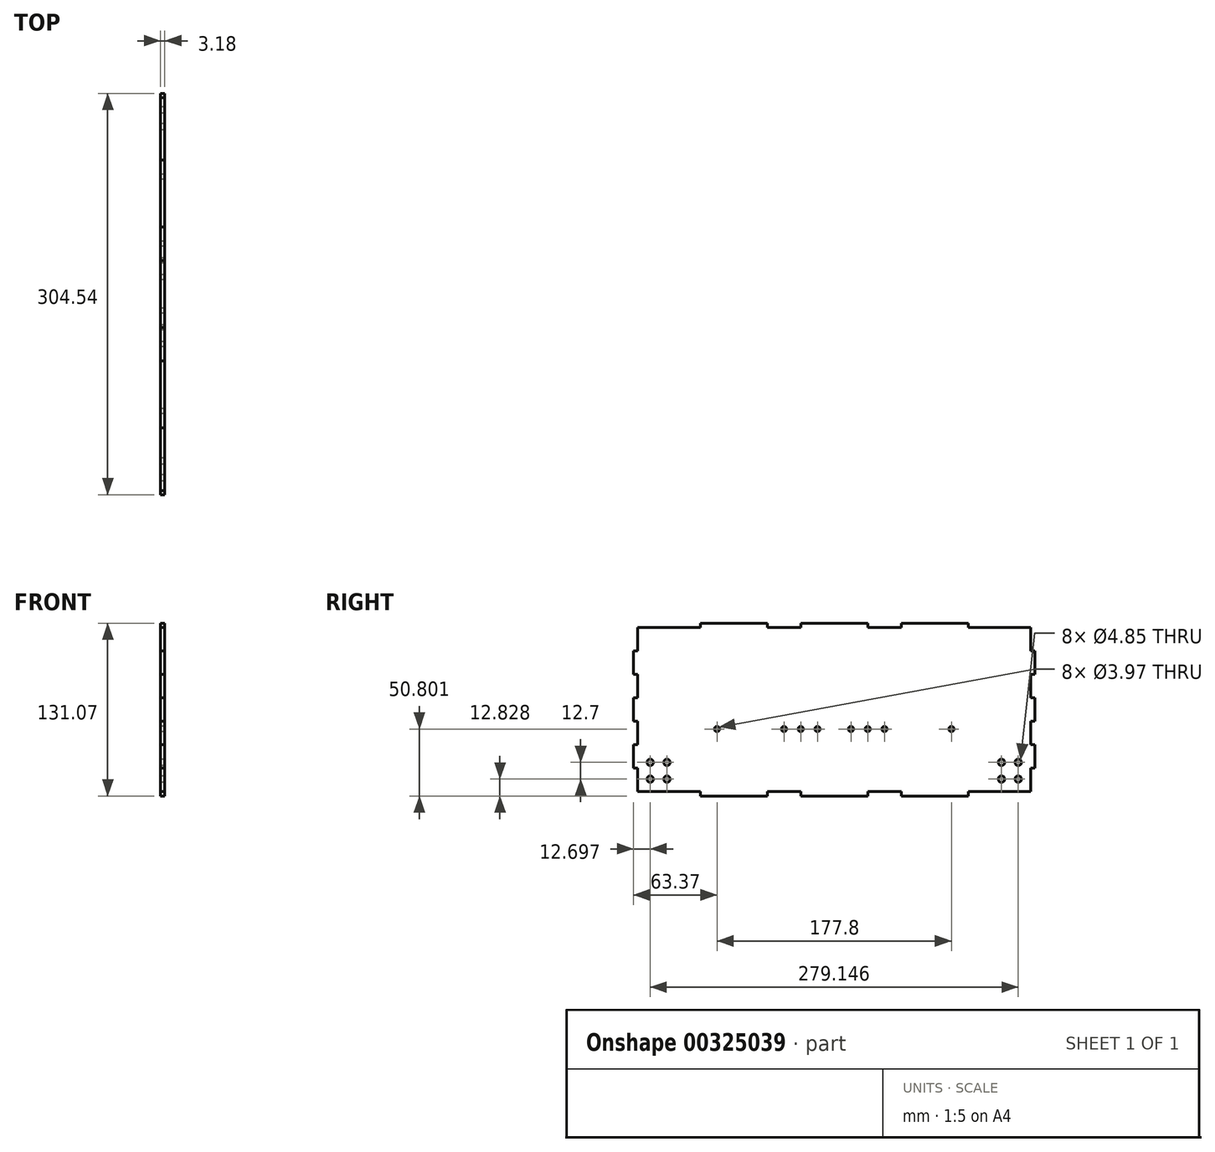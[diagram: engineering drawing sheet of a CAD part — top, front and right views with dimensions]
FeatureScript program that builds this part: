
annotation { "Feature Type Name" : "Feature", "Feature Type Description" : "" }
export const myFeature = defineFeature(function(context is Context, id is Id, definition is map)
    precondition{}
    {
        {
            var Q0;
            Q0=qCreatedBy(makeId("Right.planeOp"),FACE);
            var sketch = newSketch(context, id + "F0", { "sketchPlane" : qUnion([Q0])});
            skLineSegment(sketch, "E0.MirrorCS", {"start": v(-50.8, -81.48) * mm, "end": v(-50.8, -78.18) * mm});
            skLineSegment(sketch, "E1.MirrorCS", {"start": v(25.4, -81.48) * mm, "end": v(25.4, -78.18) * mm});
            skLineSegment(sketch, "E2.MirrorCS", {"start": v(50.8, -81.48) * mm, "end": v(50.8, -78.18) * mm});
            skLineSegment(sketch, "E3.MirrorCS", {"start": v(101.6, -81.48) * mm, "end": v(101.6, -78.18) * mm});
            skLineSegment(sketch, "E4.MirrorCS", {"start": v(-25.4, -81.48) * mm, "end": v(-25.4, -78.18) * mm});
            skLineSegment(sketch, "E5.MirrorCS", {"start": v(101.6, -81.48) * mm, "end": v(50.8, -81.48) * mm});
            skLineSegment(sketch, "E6.MirrorCS", {"start": v(-25.4, -81.48) * mm, "end": v(25.4, -81.48) * mm});
            skLineSegment(sketch, "E7.MirrorCS", {"start": v(-50.8, -81.48) * mm, "end": v(-25.4, -81.48) * mm, "construction": true});
            skLineSegment(sketch, "E8.MirrorCS", {"start": v(-101.6, -81.48) * mm, "end": v(-50.8, -81.48) * mm});
            skLineSegment(sketch, "E9.MirrorCS", {"start": v(-101.6, -81.48) * mm, "end": v(-101.6, -78.18) * mm});
            skLineSegment(sketch, "E10", {"start": v(101.6, -78.18) * mm, "end": v(149.1, -78.18) * mm});
            skLineSegment(sketch, "E11", {"start": v(50.8, -78.18) * mm, "end": v(25.4, -78.18) * mm});
            skLineSegment(sketch, "E12", {"start": v(-25.4, -78.18) * mm, "end": v(-50.8, -78.18) * mm});
            skLineSegment(sketch, "E13.MirrorCS", {"start": v(-101.6, -78.18) * mm, "end": v(-149.1, -78.18) * mm});
            skLineSegment(sketch, "E14", {"start": v(-149.1, -78.18) * mm, "end": v(-149.1, -60.4) * mm});
            skLineSegment(sketch, "E15", {"start": v(149.1, 46.28) * mm, "end": v(149.1, 28.5) * mm});
            skLineSegment(sketch, "E16", {"start": v(149.1, -15.95) * mm, "end": v(-149.1, -15.95) * mm, "construction": true});
            skLineSegment(sketch, "E17.MirrorCS", {"start": v(-50.8, 49.59) * mm, "end": v(-25.4, 49.59) * mm, "construction": true});
            skLineSegment(sketch, "E18.MirrorCS", {"start": v(-101.6, 49.59) * mm, "end": v(-101.6, 46.28) * mm});
            skLineSegment(sketch, "E19.MirrorCS", {"start": v(50.8, 46.28) * mm, "end": v(25.4, 46.28) * mm});
            skLineSegment(sketch, "E20.MirrorCS", {"start": v(25.4, 49.59) * mm, "end": v(25.4, 46.28) * mm});
            skLineSegment(sketch, "E21.MirrorCS", {"start": v(101.6, 49.59) * mm, "end": v(101.6, 46.28) * mm});
            skLineSegment(sketch, "E22.MirrorCS", {"start": v(101.6, 49.59) * mm, "end": v(50.8, 49.59) * mm});
            skLineSegment(sketch, "E23.MirrorCS", {"start": v(-101.6, 49.59) * mm, "end": v(-50.8, 49.59) * mm});
            skLineSegment(sketch, "E24.MirrorCS", {"start": v(-25.4, 46.28) * mm, "end": v(-50.8, 46.28) * mm});
            skLineSegment(sketch, "E25.MirrorCS", {"start": v(-101.6, 46.28) * mm, "end": v(-149.1, 46.28) * mm});
            skLineSegment(sketch, "E26.MirrorCS", {"start": v(101.6, 46.28) * mm, "end": v(149.1, 46.28) * mm});
            skLineSegment(sketch, "E27.MirrorCS", {"start": v(-50.8, 49.59) * mm, "end": v(-50.8, 46.28) * mm});
            skLineSegment(sketch, "E28.MirrorCS", {"start": v(50.8, 49.59) * mm, "end": v(50.8, 46.28) * mm});
            skLineSegment(sketch, "E29.MirrorCS", {"start": v(-25.4, 49.59) * mm, "end": v(-25.4, 46.28) * mm});
            skLineSegment(sketch, "E30.MirrorCS", {"start": v(-25.4, 49.59) * mm, "end": v(25.4, 49.59) * mm});
            skPoint(sketch, "E31", {"position": v(0, -30.68) * mm});
            skPoint(sketch, "E32", {"position": v(0, -15.95) * mm});
            skCircle(sketch, "E33", {"center": v(38.1, -30.68) * mm, "radius": 1.98 * mm});
            skCircle(sketch, "E34.MirrorC", {"center": v(-38.1, -30.68) * mm, "radius": 1.98 * mm});
            skCircle(sketch, "E35", {"center": v(88.9, -30.68) * mm, "radius": 1.98 * mm});
            skCircle(sketch, "E36.MirrorC", {"center": v(-88.9, -30.68) * mm, "radius": 1.98 * mm});
            skLineSegment(sketch, "E37", {"start": v(-149.1, 28.5) * mm, "end": v(-152.27, 28.5) * mm});
            skLineSegment(sketch, "E38", {"start": v(-152.27, 28.5) * mm, "end": v(-152.27, 10.72) * mm});
            skLineSegment(sketch, "E39", {"start": v(-152.27, 10.72) * mm, "end": v(-149.1, 10.72) * mm});
            skLineSegment(sketch, "E40", {"start": v(-149.1, -7.06) * mm, "end": v(-152.27, -7.06) * mm});
            skLineSegment(sketch, "E41", {"start": v(-152.27, -7.06) * mm, "end": v(-152.27, -24.84) * mm});
            skLineSegment(sketch, "E42", {"start": v(-152.27, -24.84) * mm, "end": v(-149.1, -24.84) * mm});
            skLineSegment(sketch, "E43", {"start": v(-149.1, -42.62) * mm, "end": v(-152.27, -42.62) * mm});
            skLineSegment(sketch, "E44", {"start": v(-152.27, -42.62) * mm, "end": v(-152.27, -60.4) * mm});
            skLineSegment(sketch, "E45", {"start": v(-152.27, -60.4) * mm, "end": v(-149.1, -60.4) * mm});
            skLineSegment(sketch, "E46", {"start": v(-152.27, 10.72) * mm, "end": v(-152.27, -7.06) * mm, "construction": true});
            skLineSegment(sketch, "E47", {"start": v(-152.27, -24.84) * mm, "end": v(-152.27, -42.62) * mm, "construction": true});
            skLineSegment(sketch, "E48", {"start": v(-152.27, 28.5) * mm, "end": v(-152.27, 46.28) * mm, "construction": true});
            skLineSegment(sketch, "E49", {"start": v(-152.27, -60.4) * mm, "end": v(-152.27, -78.18) * mm, "construction": true});
            skLineSegment(sketch, "E50.trimOffspring", {"start": v(-149.1, 28.5) * mm, "end": v(-149.1, 46.28) * mm});
            skLineSegment(sketch, "E51.trimOffspring", {"start": v(-149.1, -7.06) * mm, "end": v(-149.1, 10.72) * mm});
            skLineSegment(sketch, "E52.trimOffspring", {"start": v(-149.1, -42.62) * mm, "end": v(-149.1, -24.84) * mm});
            skLineSegment(sketch, "E53.MirrorCS", {"start": v(152.27, 10.72) * mm, "end": v(152.27, -7.06) * mm, "construction": true});
            skLineSegment(sketch, "E54.MirrorCS", {"start": v(149.1, -42.62) * mm, "end": v(149.1, -24.84) * mm});
            skLineSegment(sketch, "E55.MirrorCS", {"start": v(152.27, 28.5) * mm, "end": v(152.27, 10.72) * mm});
            skLineSegment(sketch, "E56.MirrorCS", {"start": v(152.27, -24.84) * mm, "end": v(152.27, -42.62) * mm, "construction": true});
            skLineSegment(sketch, "E57.MirrorCS", {"start": v(152.27, 10.72) * mm, "end": v(149.1, 10.72) * mm});
            skLineSegment(sketch, "E58.MirrorCS", {"start": v(149.1, -7.06) * mm, "end": v(152.27, -7.06) * mm});
            skLineSegment(sketch, "E59.MirrorCS", {"start": v(152.27, -7.06) * mm, "end": v(152.27, -24.84) * mm});
            skLineSegment(sketch, "E60.MirrorCS", {"start": v(152.27, -24.84) * mm, "end": v(149.1, -24.84) * mm});
            skLineSegment(sketch, "E61.MirrorCS", {"start": v(149.1, -42.62) * mm, "end": v(152.27, -42.62) * mm});
            skLineSegment(sketch, "E62.MirrorCS", {"start": v(149.1, -7.06) * mm, "end": v(149.1, 10.72) * mm});
            skLineSegment(sketch, "E63.MirrorCS", {"start": v(152.27, -42.62) * mm, "end": v(152.27, -60.4) * mm});
            skLineSegment(sketch, "E64.MirrorCS", {"start": v(152.27, -60.4) * mm, "end": v(149.1, -60.4) * mm});
            skLineSegment(sketch, "E65.MirrorCS", {"start": v(149.1, 28.5) * mm, "end": v(152.27, 28.5) * mm});
            skLineSegment(sketch, "E66.trimOffspring", {"start": v(149.1, 10.72) * mm, "end": v(149.1, -7.06) * mm});
            skPoint(sketch, "E67.orphan", {"position": v(149.1, -15.95) * mm});
            skLineSegment(sketch, "E68.trimOffspring", {"start": v(149.1, -15.95) * mm, "end": v(149.1, -42.62) * mm});
            skLineSegment(sketch, "E69.trimOffspring", {"start": v(149.1, -60.4) * mm, "end": v(149.1, -78.18) * mm});
            skCircle(sketch, "E70", {"center": v(25.4, -30.68) * mm, "radius": 1.98 * mm});
            skCircle(sketch, "E71", {"center": v(12.7, -30.68) * mm, "radius": 1.98 * mm});
            skCircle(sketch, "E72", {"center": v(-25.4, -30.68) * mm, "radius": 1.98 * mm});
            skCircle(sketch, "E73", {"center": v(-12.7, -30.68) * mm, "radius": 1.98 * mm});
            skCircle(sketch, "E74", {"center": v(-139.57, -68.65) * mm, "radius": 2.42 * mm});
            skCircle(sketch, "E75", {"center": v(-126.87, -68.65) * mm, "radius": 2.42 * mm});
            skCircle(sketch, "E76", {"center": v(-126.87, -55.95) * mm, "radius": 2.42 * mm});
            skCircle(sketch, "E77", {"center": v(-139.57, -55.95) * mm, "radius": 2.42 * mm});
            skCircle(sketch, "E78.MirrorC", {"center": v(126.87, -55.95) * mm, "radius": 2.42 * mm});
            skCircle(sketch, "E79.MirrorC", {"center": v(126.87, -68.65) * mm, "radius": 2.42 * mm});
            skCircle(sketch, "E80.MirrorC", {"center": v(139.57, -68.65) * mm, "radius": 2.42 * mm});
            skCircle(sketch, "E81.MirrorC", {"center": v(139.57, -55.95) * mm, "radius": 2.42 * mm});
            skSolve(sketch);
        }
        {
            var Q0;
            Q0=makeQuery(id+"F0.imprint","IMPRINT",FACE,{"disambiguationData":[TD([[makeQuery(id+"F0.imprint","IMPRINT",EDGE,{"derivedFrom":sQuery(id+"F0.wireOp",EDGE,"E0.MirrorCS")}),1.0]])]});
            extrude(context, id + "F1", {"entities" : qUnion([Q0]), "depth" : 3.17 * mm});
        }
    });
